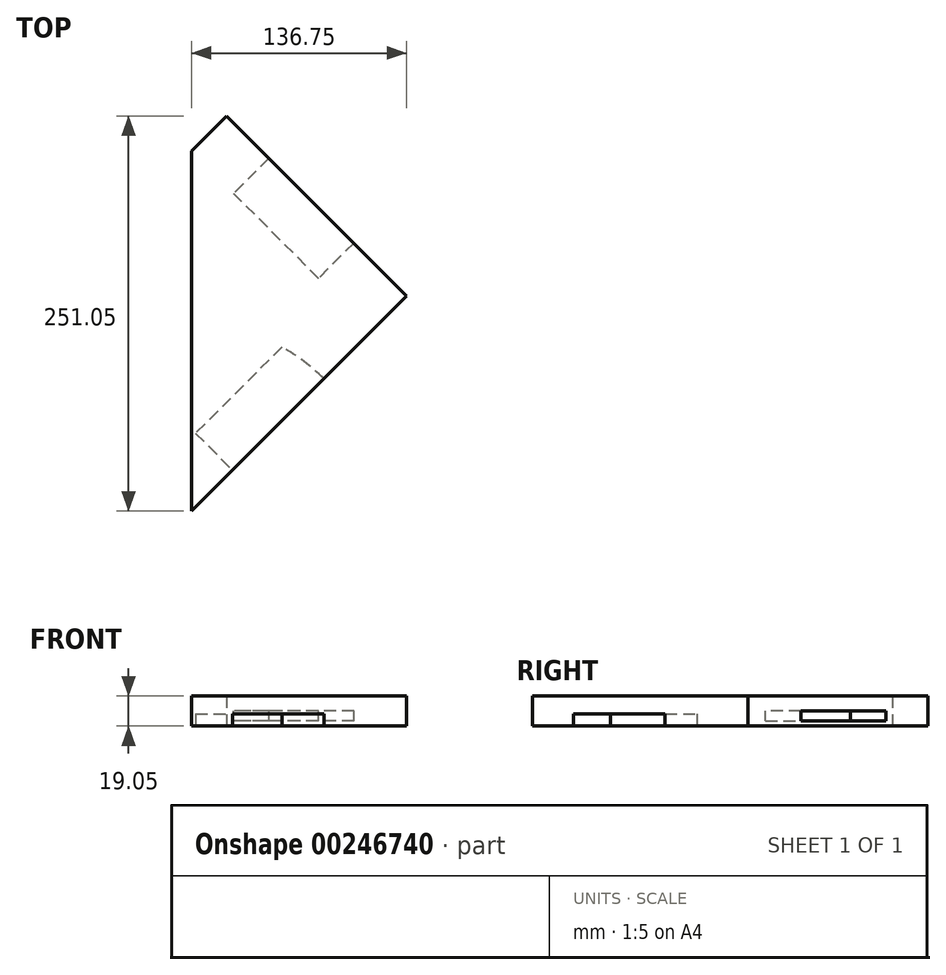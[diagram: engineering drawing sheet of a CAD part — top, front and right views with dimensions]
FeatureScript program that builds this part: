
annotation { "Feature Type Name" : "Feature", "Feature Type Description" : "" }
export const myFeature = defineFeature(function(context is Context, id is Id, definition is map)
    precondition{}
    {
        {
            var Q0;
            Q0=qCreatedBy(makeId("Top.planeOp"),FACE);
            var sketch = newSketch(context, id + "F0", { "sketchPlane" : qUnion([Q0])});
            skLineSegment(sketch, "E0.bottom", {"start": v(-109.45, 125.26) * mm, "end": v(119.15, 125.26) * mm});
            skLineSegment(sketch, "E0.top", {"start": v(-109.45, -103.34) * mm, "end": v(119.15, -103.34) * mm});
            skLineSegment(sketch, "E0.left", {"start": v(-109.45, 125.26) * mm, "end": v(-109.45, -103.34) * mm});
            skLineSegment(sketch, "E0.right", {"start": v(119.15, 125.26) * mm, "end": v(119.15, -103.34) * mm});
            skSolve(sketch);
        }
        {
            var Q0;
            Q0 = qSketchRegion(id + "F0", true);
            extrude(context, id + "F1", {"entities" : qUnion([Q0]), "depth" : 19.05 * mm});
        }
        {
            var Q0;
            Q0=makeQuery(id+"F1.opExtrude","CAP_FACE",FACE,{"disambiguationData":[OSD([sQuery(id+"F0.wireOp",EDGE,"E0.bottom"),sQuery(id+"F0.wireOp",EDGE,"E0.top"),sQuery(id+"F0.wireOp",EDGE,"E0.left"),sQuery(id+"F0.wireOp",EDGE,"E0.right")])],"isStart":false});
            var sketch = newSketch(context, id + "F2", { "sketchPlane" : qUnion([Q0])});
            skLineSegment(sketch, "E1", {"start": v(119.15, 125.26) * mm, "end": v(-109.45, -103.34) * mm});
            skLineSegment(sketch, "E2", {"start": v(-109.45, -103.34) * mm, "end": v(155.72, -103.34) * mm});
            skLineSegment(sketch, "E3", {"start": v(155.72, -103.34) * mm, "end": v(119.15, 125.26) * mm});
            skSolve(sketch);
        }
        {
            var Q0;
            Q0 = qSketchRegion(id + "F2", true);
            extrude(context, id + "F3", {"entities" : qUnion([Q0]), "operationType" : NewBodyOperationType.REMOVE, "endBound" : BoundingType.THROUGH_ALL, "oppositeDirection" : true, "depth" : 127 * mm});
        }
        {
            var Q0;
            Q0=makeQuery(id+"F1.opExtrude","CAP_FACE",FACE,{"disambiguationData":[OSD([sQuery(id+"F0.wireOp",EDGE,"E0.bottom"),sQuery(id+"F0.wireOp",EDGE,"E0.top"),sQuery(id+"F0.wireOp",EDGE,"E0.left"),sQuery(id+"F0.wireOp",EDGE,"E0.right")])],"isStart":false});
            var sketch = newSketch(context, id + "F4", { "sketchPlane" : qUnion([Q0])});
            skLineSegment(sketch, "E4", {"start": v(-109.45, 125.26) * mm, "end": v(4.85, 10.96) * mm});
            skLineSegment(sketch, "E5", {"start": v(4.85, 10.96) * mm, "end": v(150.63, 139.13) * mm});
            skLineSegment(sketch, "E6", {"start": v(150.63, 139.13) * mm, "end": v(-109.45, 125.26) * mm});
            skSolve(sketch);
        }
        {
            var Q0;
            Q0 = qSketchRegion(id + "F4", true);
            extrude(context, id + "F5", {"entities" : qUnion([Q0]), "operationType" : NewBodyOperationType.REMOVE, "endBound" : BoundingType.SYMMETRIC, "oppositeDirection" : true, "depth" : 127 * mm});
        }
        {
            var Q0;
            Q0=makeQuery(id+"F5.boolean.opBoolean","COPY",FACE,{"derivedFrom":makeQuery(id+"F5.opExtrude","SWEPT_FACE",FACE,{"disambiguationData":[OSD([sQuery(id+"F4.wireOp",EDGE,"E4")])]})});
            var sketch = newSketch(context, id + "F6", { "sketchPlane" : qUnion([Q0])});
            skPoint(sketch, "E7.oppositeSnap0", {"position": v(165.96, 9.53) * mm});
            skLineSegment(sketch, "E7.bottom", {"start": v(51.8, 3.17) * mm, "end": v(128, 3.17) * mm});
            skLineSegment(sketch, "E7.top", {"start": v(51.8, 9.53) * mm, "end": v(128, 9.53) * mm});
            skLineSegment(sketch, "E7.left", {"start": v(51.8, 3.17) * mm, "end": v(51.8, 9.53) * mm});
            skLineSegment(sketch, "E7.right", {"start": v(128, 3.17) * mm, "end": v(128, 9.53) * mm});
            skSolve(sketch);
        }
        {
            var Q0;
            Q0=makeQuery(id+"F3.boolean.opBoolean","COPY",FACE,{"derivedFrom":makeQuery(id+"F3.opExtrude","SWEPT_FACE",FACE,{"disambiguationData":[OSD([sQuery(id+"F2.wireOp",EDGE,"E1")])]})});
            var sketch = newSketch(context, id + "F7", { "sketchPlane" : qUnion([Q0])});
            skLineSegment(sketch, "E8.bottom", {"start": v(-113.64, 7.62) * mm, "end": v(-36.17, 7.62) * mm});
            skLineSegment(sketch, "E8.top", {"start": v(-113.64, 0) * mm, "end": v(-36.17, 0) * mm});
            skLineSegment(sketch, "E8.left", {"start": v(-113.64, 7.62) * mm, "end": v(-113.64, 0) * mm});
            skLineSegment(sketch, "E8.right", {"start": v(-36.17, 7.62) * mm, "end": v(-36.17, 0) * mm});
            skSolve(sketch);
        }
        {
            var Q0;
            Q0=makeQuery(id+"F7.imprint","IMPRINT",FACE,{"disambiguationData":[TD([[makeQuery(id+"F7.imprint","IMPRINT",EDGE,{"derivedFrom":sQuery(id+"F7.wireOp",EDGE,"E8.bottom")}),-1.0]])]});
            extrude(context, id + "F8", {"entities" : qUnion([Q0]), "operationType" : NewBodyOperationType.REMOVE, "oppositeDirection" : true, "depth" : 33.02 * mm});
        }
        {
            var Q0;
            Q0=makeQuery(id+"F6.imprint","IMPRINT",FACE,{"disambiguationData":[TD([[makeQuery(id+"F6.imprint","IMPRINT",EDGE,{"derivedFrom":sQuery(id+"F6.wireOp",EDGE,"E7.bottom")}),-1.0]])]});
            extrude(context, id + "F9", {"entities" : qUnion([Q0]), "operationType" : NewBodyOperationType.ADD, "depth" : 31.75 * mm});
        }
        {
            var Q0;
            {var subQ0=sQuery(id+"F0.wireOp",EDGE,"E0.left");Q0=makeQuery(id+"F3.boolean.opBoolean","MERGE",VERTEX,{"derivedFrom":[makeQuery(id+"F1.opExtrude","CAP_VERTEX",VERTEX,{"disambiguationData":[OSD([sQuery(id+"F0.wireOp",EDGE,"E0.top"),subQ0])],"isStart":false}),makeQuery(id+"F3.opExtrude","CAP_VERTEX",VERTEX,{"disambiguationData":[OSD([subQ0,sQuery(id+"F2.wireOp",EDGE,"E1"),sQuery(id+"F2.wireOp",EDGE,"E2")])],"isStart":true})]});}
            var Q1;
            Q1=makeQuery(id+"F1.opExtrude","CAP_VERTEX",VERTEX,{"disambiguationData":[OSD([sQuery(id+"F0.wireOp",EDGE,"E0.top"),sQuery(id+"F0.wireOp",EDGE,"E0.left")])],"isStart":true});
            var Q2;
            Q2=makeQuery(id+"F8.boolean.opBoolean","COPY",VERTEX,{"derivedFrom":makeQuery(id+"F8.opExtrude","CAP_VERTEX",VERTEX,{"disambiguationData":[OSD([sQuery(id+"F0.wireOp",EDGE,"E0.bottom"),sQuery(id+"F0.wireOp",EDGE,"E0.top"),sQuery(id+"F0.wireOp",EDGE,"E0.left"),sQuery(id+"F0.wireOp",EDGE,"E0.right"),sQuery(id+"F2.wireOp",EDGE,"E1"),sQuery(id+"F7.wireOp",EDGE,"E8.top"),sQuery(id+"F7.wireOp",EDGE,"E8.right")])],"isStart":false})});
            cPlane(context, id + "F10", {"entities" : qUnion([Q0, Q1, Q2]), "cplaneType" : CPlaneType.THREE_POINT, "offset" : 25.4 * mm, "width" : 152.4 * mm, "height" : 152.4 * mm});
        }
        {
            var Q0;
            Q0=qCreatedBy(id+"F10.planeOp",FACE);
            var sketch = newSketch(context, id + "F11", { "sketchPlane" : qUnion([Q0])});
            skLineSegment(sketch, "E9.bottom", {"start": v(24.38, 7.62) * mm, "end": v(58.34, 7.62) * mm});
            skLineSegment(sketch, "E9.top", {"start": v(24.38, -8.42) * mm, "end": v(58.34, -8.42) * mm});
            skLineSegment(sketch, "E9.left", {"start": v(24.38, 7.62) * mm, "end": v(24.38, -8.42) * mm});
            skLineSegment(sketch, "E9.right", {"start": v(58.34, 7.62) * mm, "end": v(58.34, -8.42) * mm});
            skSolve(sketch);
        }
        {
            var Q0;
            Q0 = qSketchRegion(id + "F11", true);
            var Q1;
            {var subQ0=sQuery(id+"F0.wireOp",EDGE,"E0.left");Q1=makeQuery(id+"F3.boolean.opBoolean","MERGE",EDGE,{"derivedFrom":[makeQuery(id+"F1.opExtrude","SWEPT_EDGE",EDGE,{"disambiguationData":[OSD([sQuery(id+"F0.wireOp",EDGE,"E0.top"),subQ0])]}),makeQuery(id+"F3.opExtrude","SWEPT_EDGE",EDGE,{"disambiguationData":[OSD([subQ0,sQuery(id+"F2.wireOp",EDGE,"E1"),sQuery(id+"F2.wireOp",EDGE,"E2")])]})]});}
            revolve(context, id + "F12", {"operationType" : NewBodyOperationType.REMOVE, "entities" : qUnion([Q0]), "axis" : qUnion([Q1]), "revolveType" : RevolveType.ONE_DIRECTION, "angle" : 35 * degree});
        }
    });
